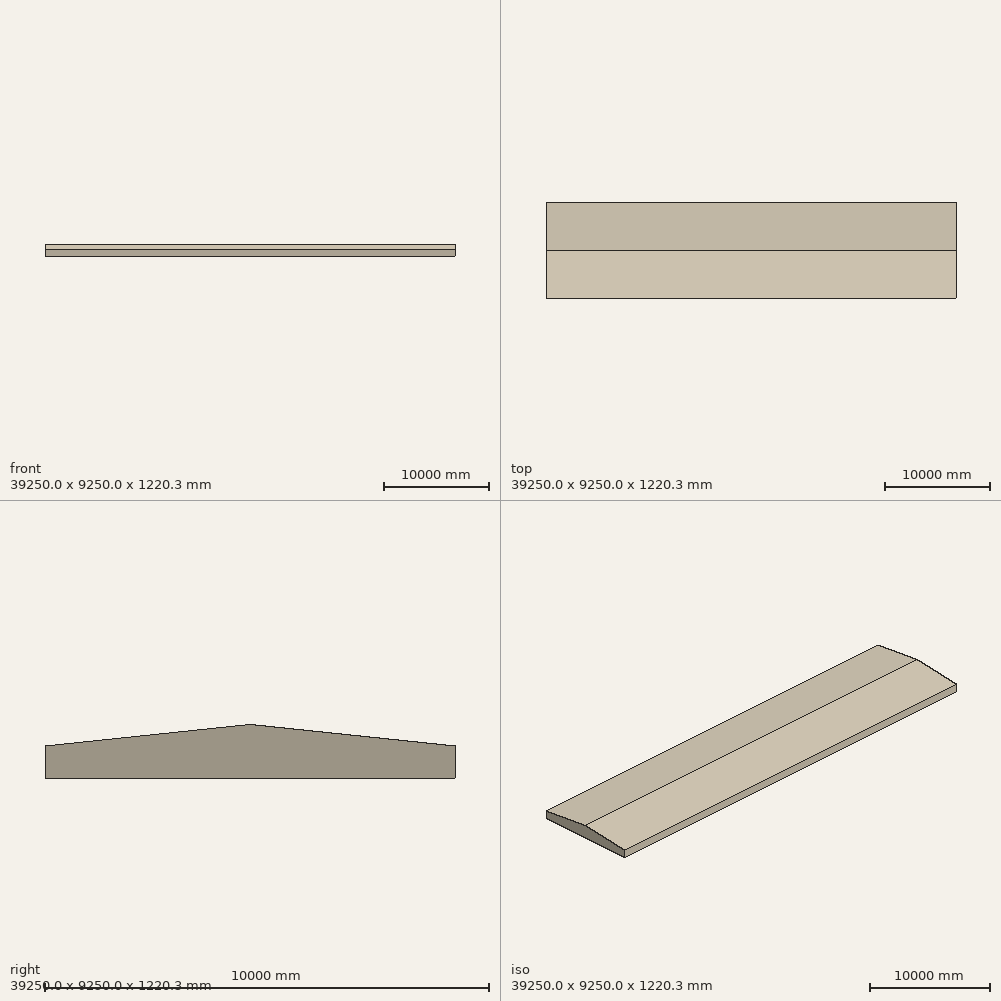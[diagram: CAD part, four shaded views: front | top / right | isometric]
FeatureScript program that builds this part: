
annotation { "Feature Type Name" : "Feature", "Feature Type Description" : "" }
export const myFeature = defineFeature(function(context is Context, id is Id, definition is map)
    precondition{}
    {
        {
            var Q0;
            Q0=qCreatedBy(makeId("Top.planeOp"),FACE);
            var sketch = newSketch(context, id + "F0", { "sketchPlane" : qUnion([Q0])});
            skLineSegment(sketch, "E0.bottom", {"start": v(0, 0) * mm, "end": v(39250, 0) * mm});
            skLineSegment(sketch, "E0.top", {"start": v(0, -9250) * mm, "end": v(39250, -9250) * mm});
            skLineSegment(sketch, "E0.left", {"start": v(0, 0) * mm, "end": v(0, -9250) * mm});
            skLineSegment(sketch, "E0.right", {"start": v(39250, 0) * mm, "end": v(39250, -9250) * mm});
            skSolve(sketch);
        }
        {
            var Q0;
            Q0=qSketchRegion(id+"F0",true);
            extrude(context, id + "F1", {"entities" : qUnion([Q0]), "depth" : 150 * mm, "offsetDistance" : 25 * mm});
        }
        {
            var Q0;
            Q0=makeQuery(id+"F1.opExtrude","CAP_FACE",FACE,{"disambiguationData":[OSD([sQuery(id+"F0.wireOp",EDGE,"E0.bottom"),sQuery(id+"F0.wireOp",EDGE,"E0.top"),sQuery(id+"F0.wireOp",EDGE,"E0.left"),sQuery(id+"F0.wireOp",EDGE,"E0.right")])],"isStart":false});
            var sketch = newSketch(context, id + "F2", { "sketchPlane" : qUnion([Q0])});
            skLineSegment(sketch, "E1.0.0", {"start": v(0, 0) * mm, "end": v(0, -9250) * mm});
            skLineSegment(sketch, "E1.0.1", {"start": v(0, -9250) * mm, "end": v(39250, -9250) * mm});
            skLineSegment(sketch, "E1.0.2", {"start": v(39250, -9250) * mm, "end": v(39250, 0) * mm});
            skLineSegment(sketch, "E1.0.3", {"start": v(39250, 0) * mm, "end": v(0, 0) * mm});
            skLineSegment(sketch, "E2.0", {"start": v(150, -150) * mm, "end": v(150, -9100) * mm});
            skLineSegment(sketch, "E2.1", {"start": v(39100, -150) * mm, "end": v(150, -150) * mm});
            skLineSegment(sketch, "E2.2", {"start": v(39100, -9100) * mm, "end": v(39100, -150) * mm});
            skLineSegment(sketch, "E2.3", {"start": v(150, -9100) * mm, "end": v(39100, -9100) * mm});
            skSolve(sketch);
        }
        {
            var Q0;
            Q0=qSketchRegion(id+"F2",true);
            extrude(context, id + "F3", {"entities" : qUnion([Q0]), "operationType" : NewBodyOperationType.ADD, "depth" : 570 * mm, "offsetDistance" : 25 * mm});
        }
        {
            var Q0;
            Q0=makeQuery(id+"F3.boolean.opBoolean","MERGE",FACE,{"derivedFrom":[makeQuery(id+"F1.opExtrude","SWEPT_FACE",FACE,{"disambiguationData":[OSD([sQuery(id+"F0.wireOp",EDGE,"E0.left")])]}),makeQuery(id+"F3.opExtrude","SWEPT_FACE",FACE,{"disambiguationData":[OSD([sQuery(id+"F2.wireOp",EDGE,"E1.0.0")])]})]});
            var sketch = newSketch(context, id + "F4", { "sketchPlane" : qUnion([Q0])});
            skLineSegment(sketch, "E3", {"start": v(4625, 150) * mm, "end": v(4625, 1170) * mm, "construction": true});
            skLineSegment(sketch, "E4", {"start": v(4625, 1170) * mm, "end": v(-659.6, 614.57) * mm});
            skLineSegment(sketch, "E5", {"start": v(-659.6, 614.57) * mm, "end": v(1956.34, 2374.17) * mm});
            skLineSegment(sketch, "E6", {"start": v(1956.34, 2374.17) * mm, "end": v(4625, 1170) * mm});
            skLineSegment(sketch, "E7.MirrorCS", {"start": v(4625, 1170) * mm, "end": v(9909.6, 614.57) * mm});
            skLineSegment(sketch, "E8.MirrorCS", {"start": v(7293.66, 2374.17) * mm, "end": v(4625, 1170) * mm});
            skLineSegment(sketch, "E9.MirrorCS", {"start": v(9909.6, 614.57) * mm, "end": v(7293.66, 2374.17) * mm});
            skSolve(sketch);
        }
        {
            var Q0;
            Q0 = qSketchRegion(id + "F4", true);
            extrude(context, id + "F5", {"entities" : qUnion([Q0]), "operationType" : NewBodyOperationType.REMOVE, "endBound" : BoundingType.THROUGH_ALL, "oppositeDirection" : true, "depth" : 25 * mm, "offsetDistance" : 25 * mm});
        }
        {
            var Q0;
            Q0=makeQuery(id+"F3.boolean.opBoolean","MERGE",FACE,{"derivedFrom":[makeQuery(id+"F1.opExtrude","SWEPT_FACE",FACE,{"disambiguationData":[OSD([sQuery(id+"F0.wireOp",EDGE,"E0.left")])]}),makeQuery(id+"F3.opExtrude","SWEPT_FACE",FACE,{"disambiguationData":[OSD([sQuery(id+"F2.wireOp",EDGE,"E1.0.0")])]})]});
            var sketch = newSketch(context, id + "F6", { "sketchPlane" : qUnion([Q0])});
            skLineSegment(sketch, "E10.0", {"start": v(4625, 150) * mm, "end": v(4625, 1170) * mm, "construction": true});
            skLineSegment(sketch, "E10.1", {"start": v(4625, 1170) * mm, "end": v(-98.98, 673.49) * mm});
            skLineSegment(sketch, "E11.0", {"start": v(4625, 1220.28) * mm, "end": v(-104.2, 723.22) * mm});
            skLineSegment(sketch, "E12", {"start": v(-98.98, 673.49) * mm, "end": v(-104.2, 723.22) * mm});
            skPoint(sketch, "E13.orphan", {"position": v(-659.6, 614.57) * mm});
            skLineSegment(sketch, "E14.MirrorCS", {"start": v(9348.98, 673.49) * mm, "end": v(9354.2, 723.22) * mm});
            skLineSegment(sketch, "E15.MirrorCS", {"start": v(4625, 1170) * mm, "end": v(9348.98, 673.49) * mm});
            skLineSegment(sketch, "E16.MirrorCS", {"start": v(4625, 1220.28) * mm, "end": v(9354.2, 723.22) * mm});
            skSolve(sketch);
        }
        {
            var Q0;
            Q0 = qSketchRegion(id + "F6", true);
            extrude(context, id + "F7", {"entities" : qUnion([Q0]), "depth" : 50 * mm, "offsetDistance" : 25 * mm, "hasSecondDirection" : true, "secondDirectionOppositeDirection" : true, "secondDirectionDepth" : 39300 * mm});
        }
        {
            var Q0;
            Q0=makeQuery(id+"F3.boolean.opBoolean","MERGE",FACE,{"derivedFrom":[makeQuery(id+"F1.opExtrude","SWEPT_FACE",FACE,{"disambiguationData":[OSD([sQuery(id+"F0.wireOp",EDGE,"E0.right")])]}),makeQuery(id+"F3.opExtrude","SWEPT_FACE",FACE,{"disambiguationData":[OSD([sQuery(id+"F2.wireOp",EDGE,"E1.0.2")])]})]});
            var sketch = newSketch(context, id + "F8", { "sketchPlane" : qUnion([Q0])});
            skLineSegment(sketch, "E17.0", {"start": v(-343.54, 720) * mm, "end": v(-8906.46, 720) * mm});
            skLineSegment(sketch, "E18.0", {"start": v(-4625, 1170) * mm, "end": v(-8906.46, 720) * mm});
            skLineSegment(sketch, "E19.0", {"start": v(-4625, 1170) * mm, "end": v(-343.54, 720) * mm});
            skPoint(sketch, "E20.orphan", {"position": v(-9348.98, 673.49) * mm});
            skPoint(sketch, "E21.orphan", {"position": v(98.98, 673.49) * mm});
            skSolve(sketch);
        }
        {
            var Q0;
            Q0 = qSketchRegion(id + "F8", true);
            extrude(context, id + "F9", {"entities" : qUnion([Q0]), "operationType" : NewBodyOperationType.ADD, "oppositeDirection" : true, "depth" : 150 * mm, "offsetDistance" : 25 * mm});
        }
        {
            var Q0;
            Q0=makeQuery(id+"F3.boolean.opBoolean","MERGE",FACE,{"derivedFrom":[makeQuery(id+"F1.opExtrude","SWEPT_FACE",FACE,{"disambiguationData":[OSD([sQuery(id+"F0.wireOp",EDGE,"E0.left")])]}),makeQuery(id+"F3.opExtrude","SWEPT_FACE",FACE,{"disambiguationData":[OSD([sQuery(id+"F2.wireOp",EDGE,"E1.0.0")])]})]});
            var sketch = newSketch(context, id + "F10", { "sketchPlane" : qUnion([Q0])});
            skLineSegment(sketch, "E22.0", {"start": v(343.54, 720) * mm, "end": v(8906.46, 720) * mm});
            skLineSegment(sketch, "E22.1", {"start": v(4625, 1170) * mm, "end": v(8906.46, 720) * mm});
            skLineSegment(sketch, "E22.2", {"start": v(4625, 1170) * mm, "end": v(343.54, 720) * mm});
            skPoint(sketch, "E22.3", {"position": v(9348.98, 673.49) * mm});
            skPoint(sketch, "E22.4", {"position": v(-98.98, 673.49) * mm});
            skSolve(sketch);
        }
        {
            var Q0;
            Q0 = qSketchRegion(id + "F10", true);
            extrude(context, id + "F11", {"entities" : qUnion([Q0]), "operationType" : NewBodyOperationType.ADD, "oppositeDirection" : true, "depth" : 150 * mm, "offsetDistance" : 25 * mm});
        }
        {
            var Q0;
            Q0=makeQuery(id+"F1.opExtrude","CAP_FACE",FACE,{"disambiguationData":[OSD([sQuery(id+"F0.wireOp",EDGE,"E0.bottom"),sQuery(id+"F0.wireOp",EDGE,"E0.top"),sQuery(id+"F0.wireOp",EDGE,"E0.left"),sQuery(id+"F0.wireOp",EDGE,"E0.right")])],"isStart":true});
            var sketch = newSketch(context, id + "F12", { "sketchPlane" : qUnion([Q0])});
            skLineSegment(sketch, "E23.bottom", {"start": v(0, 100) * mm, "end": v(-266.92, 100) * mm});
            skLineSegment(sketch, "E23.top", {"start": v(0, 1100) * mm, "end": v(-266.92, 1100) * mm});
            skLineSegment(sketch, "E23.left", {"start": v(0, 100) * mm, "end": v(0, 1100) * mm});
            skLineSegment(sketch, "E23.right", {"start": v(-266.92, 100) * mm, "end": v(-266.92, 1100) * mm});
            skSolve(sketch);
        }
        {
            var Q0;
            Q0 = qSketchRegion(id + "F12", true);
            extrude(context, id + "F13", {"entities" : qUnion([Q0]), "operationType" : NewBodyOperationType.REMOVE, "endBound" : BoundingType.THROUGH_ALL, "oppositeDirection" : true, "depth" : 25 * mm, "offsetDistance" : 25 * mm});
        }
        {
            var Q0;
            Q0=makeQuery(id+"F1.opExtrude","CAP_FACE",FACE,{"disambiguationData":[OSD([sQuery(id+"F0.wireOp",EDGE,"E0.bottom"),sQuery(id+"F0.wireOp",EDGE,"E0.top"),sQuery(id+"F0.wireOp",EDGE,"E0.left"),sQuery(id+"F0.wireOp",EDGE,"E0.right")])],"isStart":true});
            var sketch = newSketch(context, id + "F14", { "sketchPlane" : qUnion([Q0])});
            skLineSegment(sketch, "E24.0.0", {"start": v(0, 9250) * mm, "end": v(0, 0) * mm});
            skLineSegment(sketch, "E24.0.1", {"start": v(0, 0) * mm, "end": v(39250, 0) * mm});
            skLineSegment(sketch, "E24.0.2", {"start": v(39250, 0) * mm, "end": v(39250, 9250) * mm});
            skLineSegment(sketch, "E24.0.3", {"start": v(39250, 9250) * mm, "end": v(0, 9250) * mm});
            skLineSegment(sketch, "E25.bottom", {"start": v(-3932.74, 10870.37) * mm, "end": v(40762.41, 10870.37) * mm});
            skLineSegment(sketch, "E25.top", {"start": v(-3932.74, -3436.02) * mm, "end": v(40762.41, -3436.02) * mm});
            skLineSegment(sketch, "E25.left", {"start": v(-3932.74, 10870.37) * mm, "end": v(-3932.74, -3436.02) * mm});
            skLineSegment(sketch, "E25.right", {"start": v(40762.41, 10870.37) * mm, "end": v(40762.41, -3436.02) * mm});
            skSolve(sketch);
        }
        {
            var Q0;
            Q0 = qSketchRegion(id + "F14", true);
            extrude(context, id + "F15", {"entities" : qUnion([Q0]), "operationType" : NewBodyOperationType.REMOVE, "endBound" : BoundingType.THROUGH_ALL, "oppositeDirection" : true, "depth" : 25 * mm, "offsetDistance" : 25 * mm});
        }
        {
            var Q0;
            Q0=makeQuery(id+"F11.boolean.opBoolean","MERGE",FACE,{"derivedFrom":[makeQuery(id+"F3.opExtrude","SWEPT_FACE",FACE,{"disambiguationData":[OSD([sQuery(id+"F2.wireOp",EDGE,"E2.0")])]}),makeQuery(id+"F11.opExtrude","CAP_FACE",FACE,{"disambiguationData":[OSD([sQuery(id+"F10.wireOp",EDGE,"E22.0"),sQuery(id+"F10.wireOp",EDGE,"E22.1"),sQuery(id+"F10.wireOp",EDGE,"E22.2")])],"isStart":false})]});
            var sketch = newSketch(context, id + "F16", { "sketchPlane" : qUnion([Q0])});
            skLineSegment(sketch, "E26.0.0", {"start": v(-150, 150) * mm, "end": v(-150, 699.66) * mm});
            skLineSegment(sketch, "E26.0.1", {"start": v(-150, 699.66) * mm, "end": v(-4625, 1170) * mm});
            skLineSegment(sketch, "E26.0.2", {"start": v(-4625, 1170) * mm, "end": v(-9100, 699.66) * mm});
            skLineSegment(sketch, "E26.0.3", {"start": v(-9100, 699.66) * mm, "end": v(-9100, 150) * mm});
            skLineSegment(sketch, "E26.0.4", {"start": v(-9100, 150) * mm, "end": v(-150, 150) * mm});
            skSolve(sketch);
        }
        {
            var Q0;
            Q0 = qSketchRegion(id + "F16", true);
            var Q1;
            Q1=makeQuery(id+"F9.opExtrude","CAP_VERTEX",VERTEX,{"disambiguationData":[OSD([sQuery(id+"F8.wireOp",EDGE,"E18.0"),sQuery(id+"F8.wireOp",EDGE,"E19.0")])],"isStart":false});
            extrude(context, id + "F17", {"entities" : qUnion([Q0]), "endBound" : BoundingType.UP_TO_VERTEX, "depth" : 25 * mm, "endBoundEntityVertex" : qUnion([Q1]), "offsetDistance" : 25 * mm});
        }
    });
